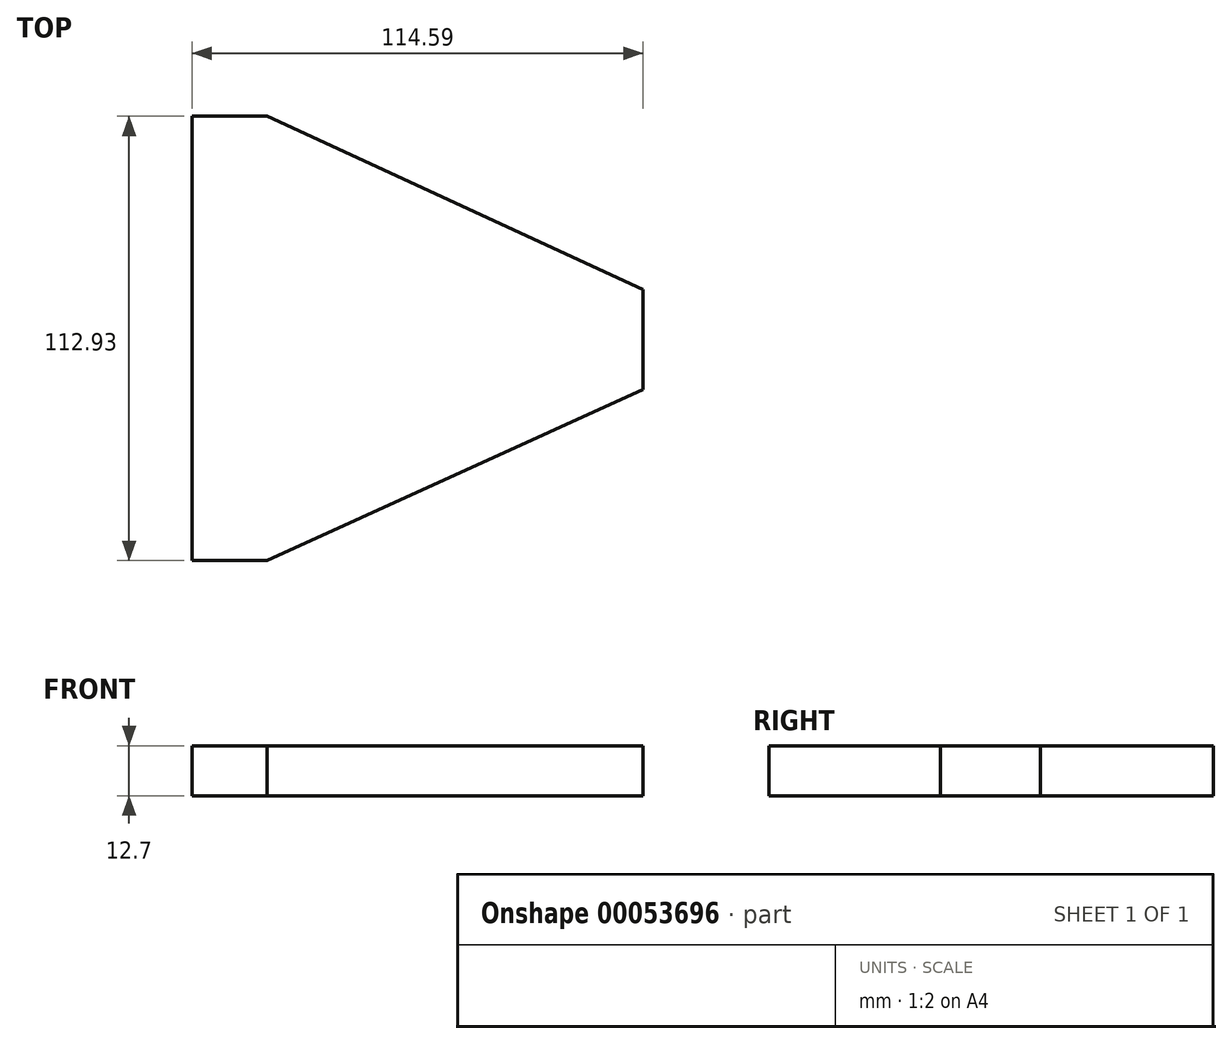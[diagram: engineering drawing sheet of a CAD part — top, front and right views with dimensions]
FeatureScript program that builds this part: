
annotation { "Feature Type Name" : "Feature", "Feature Type Description" : "" }
export const myFeature = defineFeature(function(context is Context, id is Id, definition is map)
    precondition{}
    {
        {
            var Q0;
            Q0=qCreatedBy(makeId("Top.planeOp"),FACE);
            var sketch = newSketch(context, id + "F0", { "sketchPlane" : qUnion([Q0])});
            skLineSegment(sketch, "E0", {"start": v(66.86, -12.86) * mm, "end": v(66.86, 12.54) * mm});
            skPoint(sketch, "E1", {"position": v(66.86, -0.16) * mm});
            skLineSegment(sketch, "E2", {"start": v(66.86, 12.54) * mm, "end": v(-28.68, 56.56) * mm});
            skLineSegment(sketch, "E3", {"start": v(-28.68, 56.56) * mm, "end": v(-47.73, 56.56) * mm});
            skLineSegment(sketch, "E4", {"start": v(-47.73, 56.56) * mm, "end": v(-47.73, -56.37) * mm});
            skLineSegment(sketch, "E5", {"start": v(-47.73, -56.37) * mm, "end": v(-28.68, -56.37) * mm});
            skLineSegment(sketch, "E6", {"start": v(-28.68, -56.37) * mm, "end": v(66.86, -12.86) * mm});
            skPoint(sketch, "E7", {"position": v(-47.73, 0.1) * mm});
            skSolve(sketch);
        }
        {
            var Q0;
            Q0 = qConstructionFilter(qBodyType(qCreatedBy(id + "F0" ,EDGE), BodyType.WIRE), ConstructionObject.NO);
            extrude(context, id + "F1", {"bodyType" : ToolBodyType.SURFACE, "surfaceEntities" : qUnion([Q0]), "oppositeDirection" : true, "depth" : 12.7 * mm});
        }
    });
